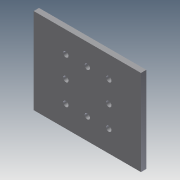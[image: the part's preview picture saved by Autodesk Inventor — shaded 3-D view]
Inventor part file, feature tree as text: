
AUTODESK INVENTOR PART (.ipt)
format: ipt  version: 2011 (Build 150239000, 239)  size: 109,568 bytes
history: native  units: in
note: dims shown in document units (in); Inventor stores cm internally (conversion verified against a paired STEP export)
features: extrude x4, sketch x4
ambient origin geometry x8: Origin, YZ Plane, XZ Plane, XY Plane, X Axis, Y Axis, Z Axis, Center Point
bodies: Solid1 (feature_tree)
feature tree (8):
  extrude  "Extrusion1"  Depth=1.1811in
  extrude  "Extrusion2"  Depth=0.315in
  extrude  "Extrusion3"  Depth=0.6299in
  extrude  "Extrusion4"  Depth=0.6299in
  sketch  "Sketch1"  dims[d0=1.5748in d1=1.1811in]
  sketch  "Sketch2"  dims[d2=0.0787in d3=0.0in d4=0.315in]
  sketch  "Sketch3"  dims[d5=0.315in d6=0.6299in]
  sketch  "Sketch4"  dims[d7=0.6299in d8=0.6299in d9=0.0787in d10=0.0787in d11=0.0in d12=0.0394in d13=0.0in d14=0.0394in d15=0.0in]
